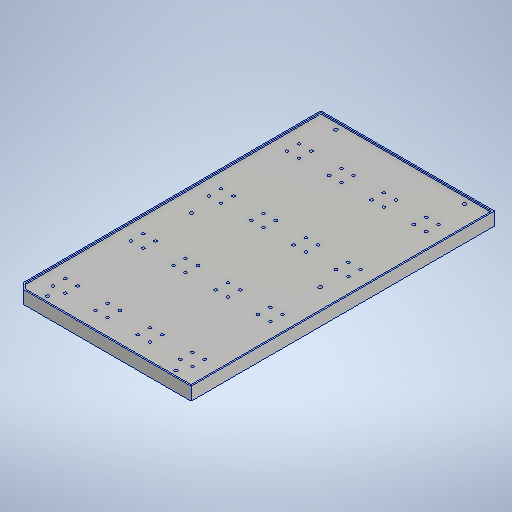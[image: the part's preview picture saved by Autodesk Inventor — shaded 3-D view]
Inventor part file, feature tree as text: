
AUTODESK INVENTOR PART (.ipt)
format: ipt  version: 2025 (Build 290162000, 162)  size: 414,720 bytes
history: native  units: in
note: dims shown in document units (in); Inventor stores cm internally (conversion verified against a paired STEP export)
features: extrude x3, sketch x2, chamfer x1, fillet x1, hole x1
ambient origin geometry x8: Origin, YZ Plane, XZ Plane, XY Plane, X Axis, Y Axis, Z Axis, Center Point
bodies: Solid1 (feature_tree)
feature tree (8):
  extrude  "Extrusion1"  Depth=8.7402in
  chamfer  "Chamfer1"  Distance=0.375in
  extrude  "Extrusion8"  Depth=0.0394in
  extrude  "Extrusion10"  Depth=0.0394in
  fillet  "Fillet3"  Radius=0.3543in
  hole  "Hole3"  [1 undecoded]
  sketch  "Sketch Rectangular Pattern1"  dims[d0=5.0in d1=8.7402in d2=0.375in d3=0.0in]
  sketch  "Sketch13"  dims[d126=0.1772in d127=0.125in d128=45.0deg d129=0.0787in d130=0.3543in d131=0.3543in d134=0.4724in d135=0.5512in d136=0.0in d137=0.0in d138=1.5748in d140=2.2441in d141=1.5748in d143=1.2205in d166=0.0394in d167=0.0394in d168=0.0394in d169=0.0394in d172=0.0394in d173=0.0in d175=0.0394in d176=1.1024in d177=0.0394in d178=0.6102in d179=0.6102in d180=0.1772in d181=0.1772in d182=0.0968in d183=0.2362in d184=0.248in d185=0.0787in d186=90.0deg d187=0.3465in d188=0.8108in]
note: 1 required parameter value undecoded (feature->parameter linkage not recoverable at this tier; creation-order binding heuristic only, values carry confidence <= 0.55)
